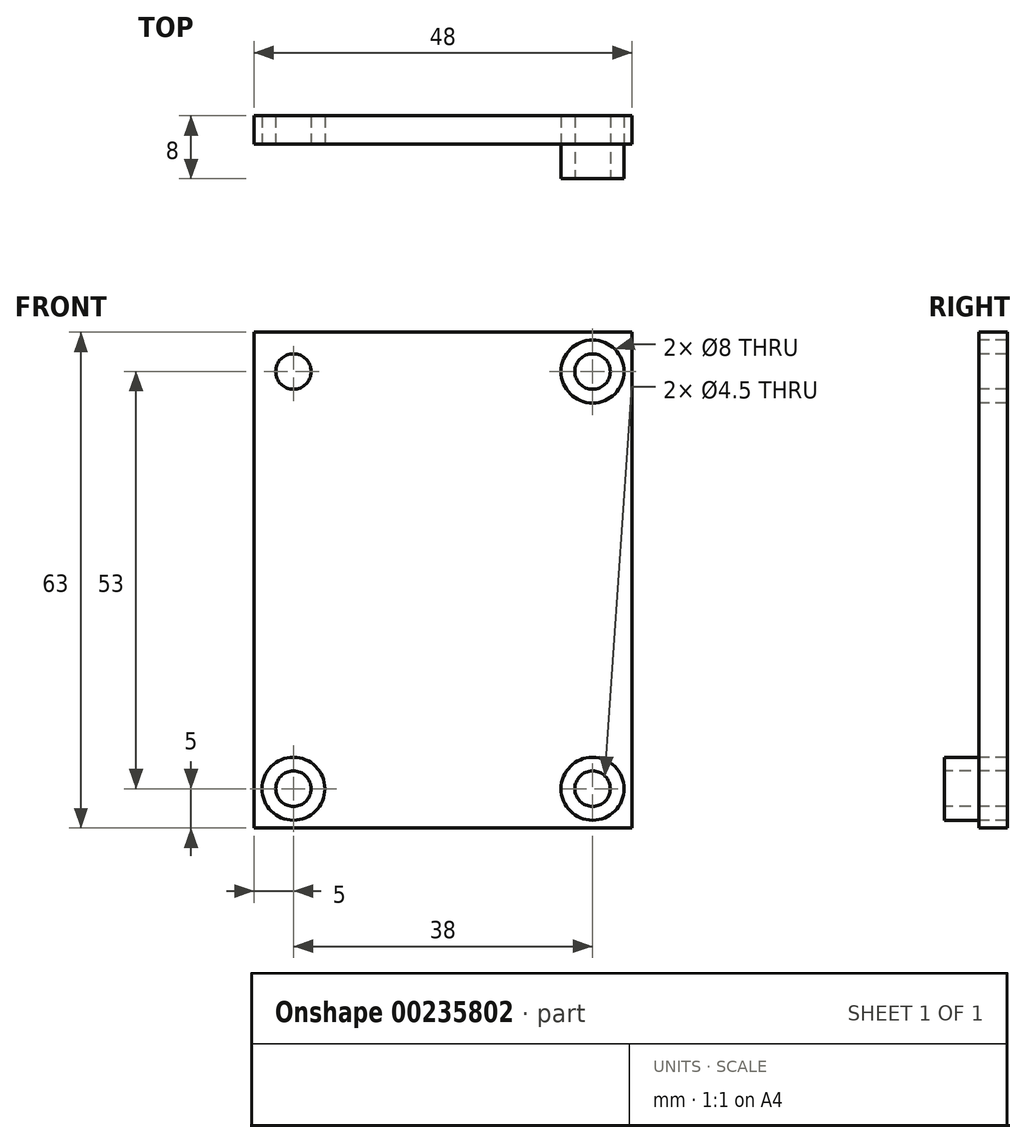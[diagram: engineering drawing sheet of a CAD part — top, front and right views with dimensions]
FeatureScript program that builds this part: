
annotation { "Feature Type Name" : "Feature", "Feature Type Description" : "" }
export const myFeature = defineFeature(function(context is Context, id is Id, definition is map)
    precondition{}
    {
        {
            var Q0;
            Q0=qCreatedBy(makeId("Front.planeOp"),FACE);
            var sketch = newSketch(context, id + "F0", { "sketchPlane" : qUnion([Q0])});
            skLineSegment(sketch, "E0", {"start": v(0, 31.5) * mm, "end": v(24, 31.5) * mm});
            skLineSegment(sketch, "E1.MirrorCS", {"start": v(0, 31.5) * mm, "end": v(-24, 31.5) * mm});
            skLineSegment(sketch, "E2.MirrorCS", {"start": v(0, -31.5) * mm, "end": v(-24, -31.5) * mm});
            skLineSegment(sketch, "E3.MirrorCS", {"start": v(0, -31.5) * mm, "end": v(24, -31.5) * mm});
            skLineSegment(sketch, "E4", {"start": v(-24, -31.5) * mm, "end": v(-24, 31.5) * mm});
            skLineSegment(sketch, "E5", {"start": v(24, -31.5) * mm, "end": v(24, 31.5) * mm});
            skSolve(sketch);
        }
        {
            var Q0;
            Q0=makeQuery(id+"F0.imprint","IMPRINT",FACE,{"disambiguationData":[TD([[makeQuery(id+"F0.imprint","IMPRINT",EDGE,{"derivedFrom":sQuery(id+"F0.wireOp",EDGE,"E0")}),-1.0]])]});
            extrude(context, id + "F1", {"entities" : qUnion([Q0]), "depth" : 8 * mm});
        }
        {
            var Q0;
            Q0=makeQuery(id+"F1.opExtrude","CAP_FACE",FACE,{"disambiguationData":[OSD([sQuery(id+"F0.wireOp",EDGE,"E0"),sQuery(id+"F0.wireOp",EDGE,"E1.MirrorCS"),sQuery(id+"F0.wireOp",EDGE,"E2.MirrorCS"),sQuery(id+"F0.wireOp",EDGE,"E3.MirrorCS"),sQuery(id+"F0.wireOp",EDGE,"E4"),sQuery(id+"F0.wireOp",EDGE,"E5")])],"isStart":false});
            var sketch = newSketch(context, id + "F2", { "sketchPlane" : qUnion([Q0])});
            skCircle(sketch, "E6", {"center": v(-19, 26.5) * mm, "radius": 2.25 * mm});
            skCircle(sketch, "E7.MirrorC", {"center": v(19, 26.5) * mm, "radius": 2.25 * mm});
            skCircle(sketch, "E8.MirrorC", {"center": v(-19, 26.5) * mm, "radius": 4 * mm});
            skCircle(sketch, "E9.MirrorC", {"center": v(19, 26.5) * mm, "radius": 4 * mm});
            skCircle(sketch, "E10.MirrorC", {"center": v(-19, -26.5) * mm, "radius": 2.25 * mm});
            skCircle(sketch, "E11.MirrorC", {"center": v(-19, -26.5) * mm, "radius": 4 * mm});
            skCircle(sketch, "E12.MirrorC", {"center": v(19, -26.5) * mm, "radius": 4 * mm});
            skCircle(sketch, "E13.MirrorC", {"center": v(19, -26.5) * mm, "radius": 2.25 * mm});
            skSolve(sketch);
        }
        {
            var Q0;
            Q0=makeQuery(id+"F2.imprint","IMPRINT",FACE,{"disambiguationData":[TD([[makeQuery(id+"F2.imprint","IMPRINT",EDGE,{"derivedFrom":sQuery(id+"F2.wireOp",EDGE,"E6")}),1.0]])]});
            var Q1;
            Q1=makeQuery(id+"F2.imprint","IMPRINT",FACE,{"disambiguationData":[TD([[makeQuery(id+"F2.imprint","IMPRINT",EDGE,{"derivedFrom":sQuery(id+"F2.wireOp",EDGE,"E7.MirrorC")}),-1.0]])]});
            var Q2;
            Q2=makeQuery(id+"F2.imprint","IMPRINT",FACE,{"disambiguationData":[TD([[makeQuery(id+"F2.imprint","IMPRINT",EDGE,{"derivedFrom":sQuery(id+"F2.wireOp",EDGE,"b92c0a81-5294-466f-a40d-21d0a3cd00420.MirrorC")}),-1.0]])]});
            var Q3;
            Q3=makeQuery(id+"F2.imprint","IMPRINT",FACE,{"disambiguationData":[TD([[makeQuery(id+"F2.imprint","IMPRINT",EDGE,{"derivedFrom":sQuery(id+"F2.wireOp",EDGE,"7b211646-67bf-4fda-8099-d619b73b96470.MirrorC")}),1.0]])]});
            extrude(context, id + "F3", {"entities" : qUnion([Q0, Q1, Q2, Q3]), "operationType" : NewBodyOperationType.REMOVE, "oppositeDirection" : true, "depth" : 2 * mm});
        }
        {
            var Q0;
            Q0=makeQuery(id+"F1.opExtrude","CAP_FACE",FACE,{"disambiguationData":[OSD([sQuery(id+"F0.wireOp",EDGE,"E0"),sQuery(id+"F0.wireOp",EDGE,"E1.MirrorCS"),sQuery(id+"F0.wireOp",EDGE,"E2.MirrorCS"),sQuery(id+"F0.wireOp",EDGE,"E3.MirrorCS"),sQuery(id+"F0.wireOp",EDGE,"E4"),sQuery(id+"F0.wireOp",EDGE,"E5")])],"isStart":false});
            var sketch = newSketch(context, id + "F4", { "sketchPlane" : qUnion([Q0])});
            skLineSegment(sketch, "E14", {"start": v(0, -28.5) * mm, "end": v(11, -28.5) * mm});
            skPoint(sketch, "E14.startSnap0", {"position": v(0, -31.5) * mm});
            skLineSegment(sketch, "E15", {"start": v(21, 0) * mm, "end": v(21, -18.5) * mm});
            skLineSegment(sketch, "E16.MirrorCS", {"start": v(21, 0) * mm, "end": v(21, 18.5) * mm});
            skLineSegment(sketch, "E17.MirrorCS", {"start": v(0, 28.5) * mm, "end": v(11, 28.5) * mm});
            skLineSegment(sketch, "E18.MirrorCS", {"start": v(0, 28.5) * mm, "end": v(-11, 28.5) * mm});
            skLineSegment(sketch, "E19.MirrorCS", {"start": v(-21, 0) * mm, "end": v(-21, 18.5) * mm});
            skLineSegment(sketch, "E20.MirrorCS", {"start": v(-21, 0) * mm, "end": v(-21, -18.5) * mm});
            skLineSegment(sketch, "E21.MirrorCS", {"start": v(0, -28.5) * mm, "end": v(-11, -28.5) * mm});
            skArc(sketch, "E22", {"start": v(-19, 20.5) * mm, "mid": v(-14.76, 22.26) * mm, "end": v(-13, 26.5) * mm});
            skArc(sketch, "E23.MirrorCS", {"start": v(19, 20.5) * mm, "mid": v(14.76, 22.26) * mm, "end": v(13, 26.5) * mm});
            skArc(sketch, "E24.MirrorCS", {"start": v(-19, -20.5) * mm, "mid": v(-14.76, -22.26) * mm, "end": v(-13, -26.5) * mm});
            skArc(sketch, "E25.MirrorCS", {"start": v(19, -20.5) * mm, "mid": v(14.76, -22.26) * mm, "end": v(13, -26.5) * mm});
            skPoint(sketch, "E26.newPointA", {"position": v(-21, 28.5) * mm});
            skPoint(sketch, "E26.newPointB", {"position": v(-22.33, 21.51) * mm});
            skArc(sketch, "E26.filletArc", {"start": v(-19, 20.5) * mm, "mid": v(-20.41, 19.91) * mm, "end": v(-21, 18.5) * mm});
            skPoint(sketch, "E27.newPointA", {"position": v(-13.34, 28.5) * mm});
            skArc(sketch, "E27.filletArc", {"start": v(-11, 28.5) * mm, "mid": v(-12.41, 27.91) * mm, "end": v(-13, 26.5) * mm});
            skPoint(sketch, "E28.newPointA", {"position": v(21, 28.5) * mm});
            skPoint(sketch, "E28.newPointB", {"position": v(13.34, 28.5) * mm});
            skArc(sketch, "E28.filletArc", {"start": v(13, 26.5) * mm, "mid": v(12.41, 27.91) * mm, "end": v(11, 28.5) * mm});
            skPoint(sketch, "E29.newPointA", {"position": v(22.33, 21.51) * mm});
            skArc(sketch, "E29.filletArc", {"start": v(21, 18.5) * mm, "mid": v(20.41, 19.91) * mm, "end": v(19, 20.5) * mm});
            skPoint(sketch, "E30.newPointA", {"position": v(-21, -28.5) * mm});
            skPoint(sketch, "E30.newPointB", {"position": v(-22.33, -21.51) * mm});
            skArc(sketch, "E30.filletArc", {"start": v(-21, -18.5) * mm, "mid": v(-20.41, -19.91) * mm, "end": v(-19, -20.5) * mm});
            skPoint(sketch, "E31.newPointA", {"position": v(-13.34, -28.5) * mm});
            skArc(sketch, "E31.filletArc", {"start": v(-13, -26.5) * mm, "mid": v(-12.41, -27.91) * mm, "end": v(-11, -28.5) * mm});
            skPoint(sketch, "E32.newPointA", {"position": v(21, -28.5) * mm});
            skPoint(sketch, "E32.newPointB", {"position": v(13.34, -28.5) * mm});
            skArc(sketch, "E32.filletArc", {"start": v(11, -28.5) * mm, "mid": v(12.41, -27.91) * mm, "end": v(13, -26.5) * mm});
            skPoint(sketch, "E33.newPointA", {"position": v(22.33, -21.51) * mm});
            skArc(sketch, "E33.filletArc", {"start": v(19, -20.5) * mm, "mid": v(20.41, -19.91) * mm, "end": v(21, -18.5) * mm});
            skSolve(sketch);
        }
        {
            var Q0;
            Q0=makeQuery(id+"F4.imprint","IMPRINT",FACE,{"disambiguationData":[TD([[makeQuery(id+"F4.imprint","IMPRINT",EDGE,{"derivedFrom":sQuery(id+"F4.wireOp",EDGE,"E14")}),1.0]])]});
            extrude(context, id + "F5", {"entities" : qUnion([Q0]), "operationType" : NewBodyOperationType.REMOVE, "oppositeDirection" : true, "depth" : 2 * mm});
        }
        {
            var Q0;
            Q0=makeQuery(id+"F5.boolean.opBoolean","COPY",FACE,{"derivedFrom":makeQuery(id+"F5.opExtrude","CAP_FACE",FACE,{"disambiguationData":[OSD([sQuery(id+"F4.wireOp",EDGE,"E14"),sQuery(id+"F4.wireOp",EDGE,"E15"),sQuery(id+"F4.wireOp",EDGE,"E16.MirrorCS"),sQuery(id+"F4.wireOp",EDGE,"E17.MirrorCS"),sQuery(id+"F4.wireOp",EDGE,"E18.MirrorCS"),sQuery(id+"F4.wireOp",EDGE,"E19.MirrorCS"),sQuery(id+"F4.wireOp",EDGE,"E20.MirrorCS"),sQuery(id+"F4.wireOp",EDGE,"E21.MirrorCS"),sQuery(id+"F4.wireOp",EDGE,"E22"),sQuery(id+"F4.wireOp",EDGE,"E23.MirrorCS"),sQuery(id+"F4.wireOp",EDGE,"E24.MirrorCS"),sQuery(id+"F4.wireOp",EDGE,"E25.MirrorCS"),sQuery(id+"F4.wireOp",EDGE,"E26.filletArc"),sQuery(id+"F4.wireOp",EDGE,"E27.filletArc"),sQuery(id+"F4.wireOp",EDGE,"E28.filletArc"),sQuery(id+"F4.wireOp",EDGE,"E29.filletArc"),sQuery(id+"F4.wireOp",EDGE,"E30.filletArc"),sQuery(id+"F4.wireOp",EDGE,"E31.filletArc"),sQuery(id+"F4.wireOp",EDGE,"E32.filletArc"),sQuery(id+"F4.wireOp",EDGE,"E33.filletArc")])],"isStart":false})});
            var sketch = newSketch(context, id + "F6", { "sketchPlane" : qUnion([Q0])});
            skLineSegment(sketch, "E34.bottom", {"start": v(15.99, -4.38) * mm, "end": v(-15.99, -4.38) * mm});
            skLineSegment(sketch, "E34.top", {"start": v(15.99, 4.38) * mm, "end": v(-15.99, 4.38) * mm});
            skLineSegment(sketch, "E34.left", {"start": v(15.99, -4.38) * mm, "end": v(15.99, 4.38) * mm});
            skLineSegment(sketch, "E34.right", {"start": v(-15.99, -4.38) * mm, "end": v(-15.99, 4.38) * mm});
            skPoint(sketch, "E34.middle", {"position": v(0, 0) * mm});
            skText(sketch, "E35", { "text": "HVCC\n", "fontName": "OpenSans-Regular.ttf"});
            const initialGuessF6  = {"E35": [-0.01599, -0.00438, 1, 0, 0.00876]};
            skSetInitialGuess(sketch, initialGuessF6);
            skSolve(sketch);
        }
        {
            var Q0;
            Q0=makeQuery(id+"F6.imprint","IMPRINT",FACE,{"disambiguationData":[TD([[makeQuery(id+"F6.imprint","IMPRINT",EDGE,{"derivedFrom":sQuery(id+"F6.wireOp",EDGE,"E35.sketch_text.stroke-0")}),-1.0]])]});
            var Q1;
            Q1=makeQuery(id+"F6.imprint","IMPRINT",FACE,{"disambiguationData":[TD([[makeQuery(id+"F6.imprint","IMPRINT",EDGE,{"derivedFrom":sQuery(id+"F6.wireOp",EDGE,"E35.sketch_text.stroke-12")}),-1.0]])]});
            var Q2;
            Q2=makeQuery(id+"F6.imprint","IMPRINT",FACE,{"disambiguationData":[TD([[makeQuery(id+"F6.imprint","IMPRINT",EDGE,{"derivedFrom":sQuery(id+"F6.wireOp",EDGE,"E35.sketch_text.stroke-21")}),-1.0]])]});
            var Q3;
            Q3=makeQuery(id+"F6.imprint","IMPRINT",FACE,{"disambiguationData":[TD([[makeQuery(id+"F6.imprint","IMPRINT",EDGE,{"derivedFrom":sQuery(id+"F6.wireOp",EDGE,"E35.sketch_text.stroke-36")}),-1.0]])]});
            var Q4;
            {var subQ0=sQuery(id+"F6.wireOp",EDGE,"E35.sketch_text.stroke-27");var subQ1=sQuery(id+"F6.wireOp",EDGE,"E34.bottom");var subQ2=makeQuery(id+"F6.imprint","INTERSECT",VERTEX,{"derivedFrom":[subQ1,subQ0]});Q4=makeQuery(id+"F6.imprint","IMPRINT",FACE,{"disambiguationData":[TD([[makeQuery(id+"F6.imprint","IMPRINT",EDGE,{"disambiguationData":[TD([[subQ2,-1.0]])],"derivedFrom":subQ1}),1.0]])]});}
            var Q5;
            {var subQ0=sQuery(id+"F6.wireOp",EDGE,"E35.sketch_text.stroke-42");var subQ1=sQuery(id+"F6.wireOp",EDGE,"E34.bottom");var subQ2=makeQuery(id+"F6.imprint","INTERSECT",VERTEX,{"derivedFrom":[subQ1,subQ0]});Q5=makeQuery(id+"F6.imprint","IMPRINT",FACE,{"disambiguationData":[TD([[makeQuery(id+"F6.imprint","IMPRINT",EDGE,{"disambiguationData":[TD([[subQ2,-1.0]])],"derivedFrom":subQ1}),1.0]])]});}
            var Q6;
            {var subQ0=sQuery(id+"F6.wireOp",EDGE,"E35.sketch_text.stroke-33");var subQ1=sQuery(id+"F6.wireOp",EDGE,"E34.top");var subQ2=makeQuery(id+"F6.imprint","INTERSECT",VERTEX,{"derivedFrom":[subQ1,subQ0]});Q6=makeQuery(id+"F6.imprint","IMPRINT",FACE,{"disambiguationData":[TD([[makeQuery(id+"F6.imprint","IMPRINT",EDGE,{"disambiguationData":[TD([[subQ2,-1.0]])],"derivedFrom":subQ1}),-1.0]])]});}
            var Q7;
            {var subQ0=sQuery(id+"F6.wireOp",EDGE,"E35.sketch_text.stroke-48");var subQ1=sQuery(id+"F6.wireOp",EDGE,"E34.top");var subQ2=makeQuery(id+"F6.imprint","INTERSECT",VERTEX,{"derivedFrom":[subQ1,subQ0]});Q7=makeQuery(id+"F6.imprint","IMPRINT",FACE,{"disambiguationData":[TD([[makeQuery(id+"F6.imprint","IMPRINT",EDGE,{"disambiguationData":[TD([[subQ2,-1.0]])],"derivedFrom":subQ1}),-1.0]])]});}
            extrude(context, id + "F7", {"entities" : qUnion([Q0, Q1, Q2, Q3, Q4, Q5, Q6, Q7]), "operationType" : NewBodyOperationType.ADD, "depth" : 2 * mm});
        }
        {
            var Q0;
            Q0=makeQuery(id+"F2.imprint","IMPRINT",FACE,{"disambiguationData":[TD([[makeQuery(id+"F2.imprint","IMPRINT",EDGE,{"derivedFrom":sQuery(id+"F2.wireOp",EDGE,"E6")}),-1.0]])]});
            var Q1;
            Q1=makeQuery(id+"F2.imprint","IMPRINT",FACE,{"disambiguationData":[TD([[makeQuery(id+"F2.imprint","IMPRINT",EDGE,{"derivedFrom":sQuery(id+"F2.wireOp",EDGE,"E7.MirrorC")}),1.0]])]});
            var Q2;
            Q2=makeQuery(id+"F2.imprint","IMPRINT",FACE,{"disambiguationData":[TD([[makeQuery(id+"F2.imprint","IMPRINT",EDGE,{"derivedFrom":sQuery(id+"F2.wireOp",EDGE,"7b211646-67bf-4fda-8099-d619b73b96470.MirrorC")}),-1.0]])]});
            var Q3;
            Q3=makeQuery(id+"F2.imprint","IMPRINT",FACE,{"disambiguationData":[TD([[makeQuery(id+"F2.imprint","IMPRINT",EDGE,{"derivedFrom":sQuery(id+"F2.wireOp",EDGE,"b92c0a81-5294-466f-a40d-21d0a3cd00420.MirrorC")}),1.0]])]});
            extrude(context, id + "F8", {"entities" : qUnion([Q0, Q1, Q2, Q3]), "operationType" : NewBodyOperationType.REMOVE, "oppositeDirection" : true, "depth" : 4.4 * mm});
        }
        {
            var Q0;
            Q0=makeQuery(id+"F2.imprint","IMPRINT",FACE,{"disambiguationData":[TD([[makeQuery(id+"F2.imprint","IMPRINT",EDGE,{"derivedFrom":sQuery(id+"F2.wireOp",EDGE,"b92c0a81-5294-466f-a40d-21d0a3cd00420.MirrorC")}),-1.0]])]});
            var Q1;
            Q1=makeQuery(id+"F2.imprint","IMPRINT",FACE,{"disambiguationData":[TD([[makeQuery(id+"F2.imprint","IMPRINT",EDGE,{"derivedFrom":sQuery(id+"F2.wireOp",EDGE,"E6")}),1.0]])]});
            var Q2;
            Q2=makeQuery(id+"F2.imprint","IMPRINT",FACE,{"disambiguationData":[TD([[makeQuery(id+"F2.imprint","IMPRINT",EDGE,{"derivedFrom":sQuery(id+"F2.wireOp",EDGE,"E7.MirrorC")}),-1.0]])]});
            var Q3;
            Q3=makeQuery(id+"F2.imprint","IMPRINT",FACE,{"disambiguationData":[TD([[makeQuery(id+"F2.imprint","IMPRINT",EDGE,{"derivedFrom":sQuery(id+"F2.wireOp",EDGE,"7b211646-67bf-4fda-8099-d619b73b96470.MirrorC")}),1.0]])]});
            extrude(context, id + "F9", {"entities" : qUnion([Q0, Q1, Q2, Q3]), "operationType" : NewBodyOperationType.REMOVE, "endBound" : BoundingType.THROUGH_ALL, "oppositeDirection" : true, "depth" : 25 * mm});
        }
        {
            var Q0;
            Q0=makeQuery(id+"F2.imprint","IMPRINT",FACE,{"disambiguationData":[TD([[makeQuery(id+"F2.imprint","IMPRINT",EDGE,{"derivedFrom":sQuery(id+"F2.wireOp",EDGE,"E10.MirrorC")}),-1.0]])]});
            var Q1;
            Q1=makeQuery(id+"F2.imprint","IMPRINT",FACE,{"disambiguationData":[TD([[makeQuery(id+"F2.imprint","IMPRINT",EDGE,{"derivedFrom":sQuery(id+"F2.wireOp",EDGE,"E13.MirrorC")}),1.0]])]});
            extrude(context, id + "F10", {"entities" : qUnion([Q0, Q1]), "operationType" : NewBodyOperationType.REMOVE, "endBound" : BoundingType.THROUGH_ALL, "oppositeDirection" : true, "depth" : 25 * mm});
        }
        {
            var Q0;
            Q0=makeQuery(id+"F2.imprint","IMPRINT",FACE,{"disambiguationData":[TD([[makeQuery(id+"F2.imprint","IMPRINT",EDGE,{"derivedFrom":sQuery(id+"F2.wireOp",EDGE,"E10.MirrorC")}),1.0]])]});
            var Q1;
            Q1=makeQuery(id+"F2.imprint","IMPRINT",FACE,{"disambiguationData":[TD([[makeQuery(id+"F2.imprint","IMPRINT",EDGE,{"derivedFrom":sQuery(id+"F2.wireOp",EDGE,"E12.MirrorC")}),-1.0]])]});
            extrude(context, id + "F11", {"entities" : qUnion([Q0, Q1]), "operationType" : NewBodyOperationType.REMOVE, "oppositeDirection" : true, "depth" : 4.4 * mm});
        }
    });
